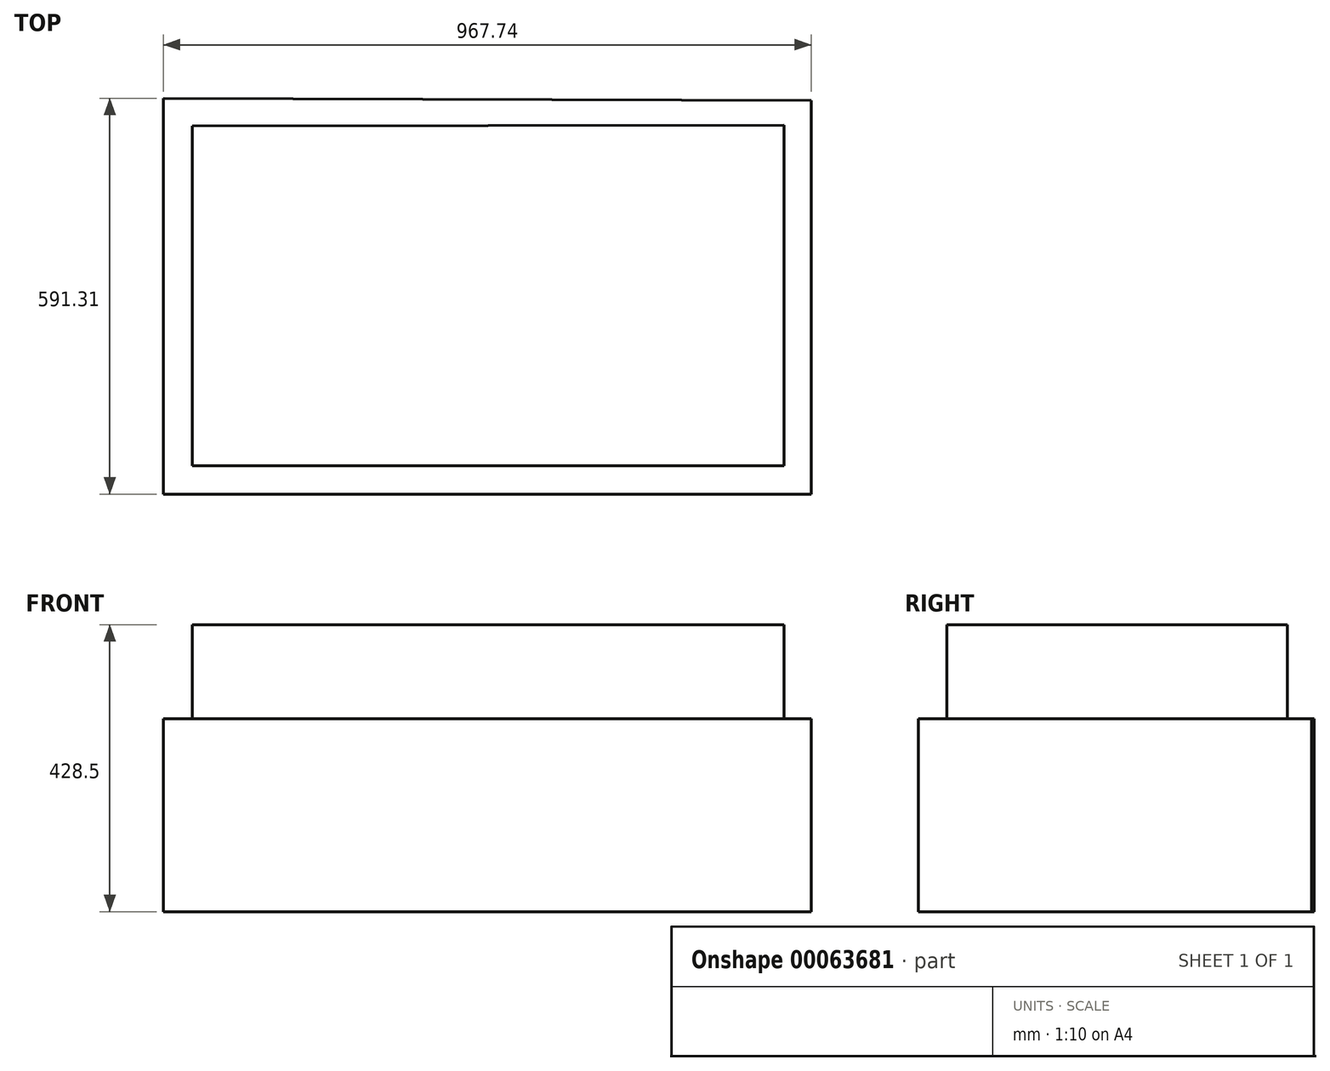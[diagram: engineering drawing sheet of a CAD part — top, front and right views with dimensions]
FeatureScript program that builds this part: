
annotation { "Feature Type Name" : "Feature", "Feature Type Description" : "" }
export const myFeature = defineFeature(function(context is Context, id is Id, definition is map)
    precondition{}
    {
        {
            var Q0;
            Q0=qCreatedBy(makeId("Top.planeOp"),FACE);
            var sketch = newSketch(context, id + "F0", { "sketchPlane" : qUnion([Q0])});
            skLineSegment(sketch, "E0", {"start": v(-505.46, 177.96) * mm, "end": v(-505.46, -413.35) * mm});
            skLineSegment(sketch, "E1", {"start": v(-505.46, -413.35) * mm, "end": v(462.28, -413.35) * mm});
            skLineSegment(sketch, "E2", {"start": v(462.28, -413.35) * mm, "end": v(462.28, 174.38) * mm});
            skLineSegment(sketch, "E3", {"start": v(462.28, 174.38) * mm, "end": v(-505.46, 177.96) * mm});
            skSolve(sketch);
        }
        {
            var Q0;
            Q0 = qSketchRegion(id + "F0", true);
            extrude(context, id + "F1", {"entities" : qUnion([Q0]), "depth" : 288.3 * mm});
        }
        {
            var Q0;
            Q0=makeQuery(id+"F1.opExtrude","CAP_FACE",FACE,{"disambiguationData":[OSD([sQuery(id+"F0.wireOp",EDGE,"E0"),sQuery(id+"F0.wireOp",EDGE,"E1"),sQuery(id+"F0.wireOp",EDGE,"E2"),sQuery(id+"F0.wireOp",EDGE,"E3")])],"isStart":false});
            var sketch = newSketch(context, id + "F2", { "sketchPlane" : qUnion([Q0])});
            skLineSegment(sketch, "E4", {"start": v(-462.4, 136.34) * mm, "end": v(-462.4, -370.9) * mm});
            skLineSegment(sketch, "E5", {"start": v(-462.4, -370.9) * mm, "end": v(421.52, -370.9) * mm});
            skLineSegment(sketch, "E6", {"start": v(421.52, -370.9) * mm, "end": v(421.52, 137.83) * mm});
            skLineSegment(sketch, "E7", {"start": v(421.52, 137.83) * mm, "end": v(-462.4, 136.34) * mm});
            skSolve(sketch);
        }
        {
            var Q0;
            Q0 = qSketchRegion(id + "F2", true);
            extrude(context, id + "F3", {"entities" : qUnion([Q0]), "operationType" : NewBodyOperationType.ADD, "depth" : 140.2 * mm});
        }
    });
